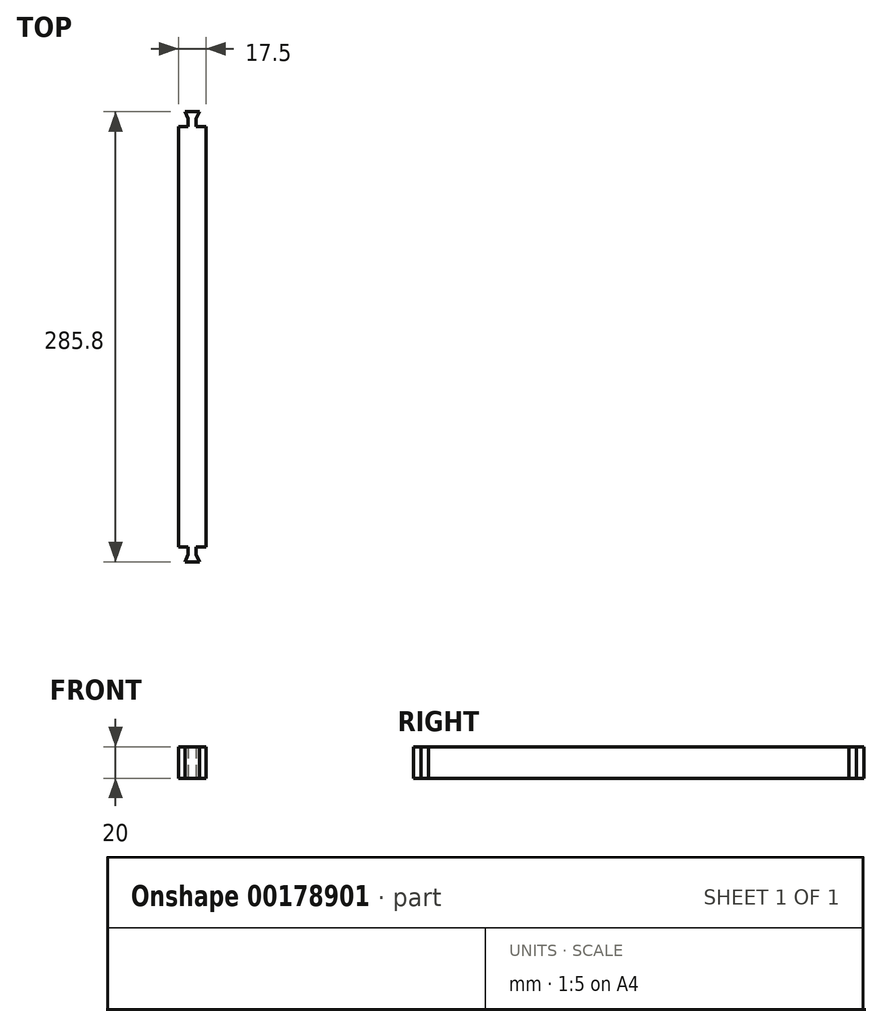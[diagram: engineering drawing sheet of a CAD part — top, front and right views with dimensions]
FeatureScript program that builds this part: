
annotation { "Feature Type Name" : "Feature", "Feature Type Description" : "" }
export const myFeature = defineFeature(function(context is Context, id is Id, definition is map)
    precondition{}
    {
        {
            var Q0;
            Q0=qCreatedBy(makeId("Top.planeOp"),FACE);
            var sketch = newSketch(context, id + "F0", { "sketchPlane" : qUnion([Q0])});
            skLineSegment(sketch, "E0.trimOffspring", {"start": v(3, 7.47) * mm, "end": v(9, 7.47) * mm});
            skLineSegment(sketch, "E1", {"start": v(3, 3.47) * mm, "end": v(3, 7.47) * mm});
            skLineSegment(sketch, "E2", {"start": v(9, 7.47) * mm, "end": v(9, -10.53) * mm});
            skLineSegment(sketch, "E3", {"start": v(3, 3.47) * mm, "end": v(5.3, -1.76) * mm});
            skLineSegment(sketch, "E4", {"start": v(5.3, -1.76) * mm, "end": v(0, -1.76) * mm});
            skLineSegment(sketch, "E5", {"start": v(9, -10.53) * mm, "end": v(0, -10.53) * mm});
            skLineSegment(sketch, "E6.MirrorCS", {"start": v(-3, 7.47) * mm, "end": v(-9, 7.47) * mm});
            skLineSegment(sketch, "E7.MirrorCS", {"start": v(-9, -10.53) * mm, "end": v(0, -10.53) * mm});
            skLineSegment(sketch, "E8.MirrorCS", {"start": v(-5.3, -1.76) * mm, "end": v(0, -1.76) * mm});
            skLineSegment(sketch, "E9.MirrorCS", {"start": v(-3, 3.47) * mm, "end": v(-3, 7.47) * mm});
            skLineSegment(sketch, "E10.MirrorCS", {"start": v(-9, 7.47) * mm, "end": v(-9, -10.53) * mm});
            skLineSegment(sketch, "E11.MirrorCS", {"start": v(-3, 3.47) * mm, "end": v(-5.3, -1.76) * mm});
            skSolve(sketch);
        }
        {
            var Q0;
            Q0=makeQuery(id+"F0.imprint","IMPRINT",FACE,{"disambiguationData":[TD([[makeQuery(id+"F0.imprint","IMPRINT",EDGE,{"derivedFrom":sQuery(id+"F0.wireOp",EDGE,"E0.trimOffspring")}),-1.0]])]});
            var sketch = newSketch(context, id + "F1", { "sketchPlane" : qUnion([Q0])});
            skLineSegment(sketch, "E12", {"start": v(0, -1) * mm, "end": v(4.5, -1) * mm});
            skLineSegment(sketch, "E13", {"start": v(2.53, 3.47) * mm, "end": v(4.5, -1) * mm});
            skLineSegment(sketch, "E14", {"start": v(2.53, 3.47) * mm, "end": v(2.53, 8.46) * mm});
            skLineSegment(sketch, "E15.MirrorCS", {"start": v(-2.53, 3.47) * mm, "end": v(-4.5, -1) * mm});
            skLineSegment(sketch, "E16.MirrorCS", {"start": v(-2.53, 3.47) * mm, "end": v(-2.53, 8.46) * mm});
            skLineSegment(sketch, "E17.MirrorCS", {"start": v(0, -1) * mm, "end": v(-4.5, -1) * mm});
            skPoint(sketch, "E18", {"position": v(8.75, 13.7) * mm});
            skLineSegment(sketch, "E19", {"start": v(8.75, 13.7) * mm, "end": v(8.75, 141.89) * mm});
            skLineSegment(sketch, "E20", {"start": v(2.53, 8.46) * mm, "end": v(8.75, 8.46) * mm});
            skLineSegment(sketch, "E21", {"start": v(8.75, 8.46) * mm, "end": v(8.75, 13.7) * mm});
            skPoint(sketch, "E22.2.internal.orphan", {"position": v(8.75, 31.02) * mm});
            skPoint(sketch, "E22.3.internal.orphan", {"position": v(8.75, 30.99) * mm});
            skPoint(sketch, "E23.MirrorP", {"position": v(-8.75, 30.99) * mm});
            skPoint(sketch, "E24.MirrorP", {"position": v(-8.75, 31.02) * mm});
            skLineSegment(sketch, "E25.MirrorCS", {"start": v(-8.75, 8.46) * mm, "end": v(-8.75, 13.7) * mm});
            skLineSegment(sketch, "E26.MirrorCS", {"start": v(-2.53, 8.46) * mm, "end": v(-8.75, 8.46) * mm});
            skLineSegment(sketch, "E27.MirrorCS", {"start": v(-8.75, 13.7) * mm, "end": v(-8.75, 141.89) * mm});
            skPoint(sketch, "E28.MirrorP", {"position": v(-8.75, 13.7) * mm});
            skPoint(sketch, "E29.start.orphan", {"position": v(0, 3.47) * mm});
            skLineSegment(sketch, "E30", {"start": v(-140.02, 141.89) * mm, "end": v(132.82, 141.89) * mm});
            skLineSegment(sketch, "E31.MirrorCS", {"start": v(0, 284.79) * mm, "end": v(-4.5, 284.79) * mm});
            skLineSegment(sketch, "E32.MirrorCS", {"start": v(-2.53, 280.3) * mm, "end": v(-2.53, 275.32) * mm});
            skLineSegment(sketch, "E33.MirrorCS", {"start": v(-2.53, 280.3) * mm, "end": v(-4.5, 284.79) * mm});
            skLineSegment(sketch, "E34.MirrorCS", {"start": v(2.53, 275.32) * mm, "end": v(8.75, 275.32) * mm});
            skLineSegment(sketch, "E35.MirrorCS", {"start": v(2.53, 280.3) * mm, "end": v(2.53, 275.32) * mm});
            skLineSegment(sketch, "E36.MirrorCS", {"start": v(2.53, 280.3) * mm, "end": v(4.5, 284.79) * mm});
            skLineSegment(sketch, "E37.MirrorCS", {"start": v(0, 284.79) * mm, "end": v(4.5, 284.79) * mm});
            skLineSegment(sketch, "E38.MirrorCS", {"start": v(-2.53, 275.32) * mm, "end": v(-8.75, 275.32) * mm});
            skLineSegment(sketch, "E39.MirrorCS", {"start": v(-8.75, 275.32) * mm, "end": v(-8.75, 270.08) * mm});
            skLineSegment(sketch, "E40.MirrorCS", {"start": v(8.75, 275.32) * mm, "end": v(8.75, 270.08) * mm});
            skPoint(sketch, "E41.MirrorP", {"position": v(0, 280.3) * mm});
            skPoint(sketch, "E42.MirrorP", {"position": v(8.75, 252.76) * mm});
            skPoint(sketch, "E43.MirrorP", {"position": v(-8.75, 252.8) * mm});
            skLineSegment(sketch, "E44.MirrorCS", {"start": v(8.75, 270.08) * mm, "end": v(8.75, 141.89) * mm});
            skLineSegment(sketch, "E45.MirrorCS", {"start": v(-8.75, 270.08) * mm, "end": v(-8.75, 141.89) * mm});
            skPoint(sketch, "E46.MirrorP", {"position": v(8.75, 270.08) * mm});
            skPoint(sketch, "E47.MirrorP", {"position": v(-8.75, 270.08) * mm});
            skPoint(sketch, "E48.MirrorP", {"position": v(8.75, 252.8) * mm});
            skPoint(sketch, "E49.MirrorP", {"position": v(-8.75, 252.76) * mm});
            skLineSegment(sketch, "E50", {"start": v(8.73, -1.14) * mm, "end": v(8.73, 0.5) * mm});
            skLineSegment(sketch, "E51", {"start": v(-2.53, 3.47) * mm, "end": v(-2.53, -1) * mm});
            skPoint(sketch, "E51.endSnap0", {"position": v(-2.25, -1) * mm});
            skSolve(sketch);
        }
        {
            var Q0;
            Q0 = qSketchRegion(id + "F1", true);
            extrude(context, id + "F2", {"entities" : qUnion([Q0]), "depth" : 20 * mm});
        }
    });
